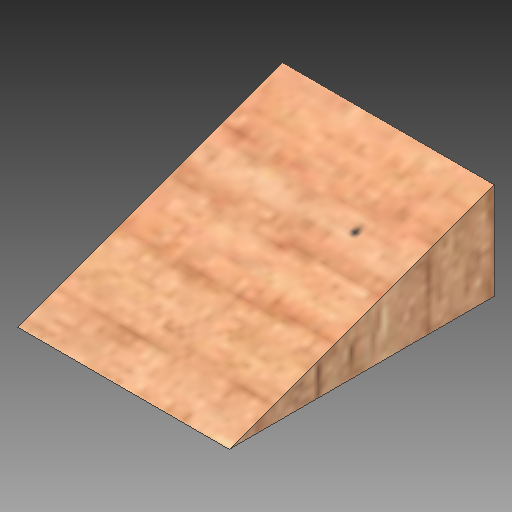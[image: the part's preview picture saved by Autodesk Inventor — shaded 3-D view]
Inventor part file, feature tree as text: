
AUTODESK INVENTOR PART (.ipt)
format: ipt  version: 2017 (Build 210142000, 142)  size: 260,608 bytes
history: native  units: in
note: dims shown in document units (in); Inventor stores cm internally (conversion verified against a paired STEP export)
features: move_body x2, extrude x1, sketch x1
ambient origin geometry x8: Origin, YZ Plane, XZ Plane, XY Plane, X Axis, Y Axis, Z Axis, Center Point
bodies: Solid1 (feature_tree)
feature tree (4):
  extrude  "Extrusion1"  Depth=1.5in
  move_body  "Move Body1"
  move_body  "Move Body2"
  sketch  "Sketch1"  dims[d2=2.0in d4=0.481in d5=1.5in d6=0.0in d7=180.0deg d8=270.0deg]
